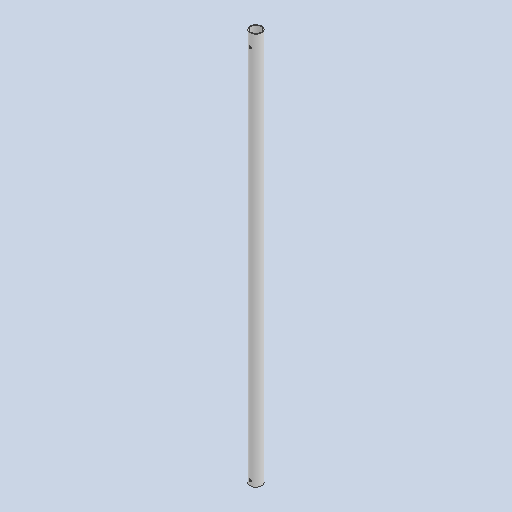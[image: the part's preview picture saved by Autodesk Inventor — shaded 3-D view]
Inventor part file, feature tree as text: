
AUTODESK INVENTOR PART (.ipt)
format: ipt  version: 2022 (Build 260153000, 153)  size: 155,648 bytes
history: native  units: mm
features: extrude x2, sketch x2
ambient origin geometry x8: Origin, YZ Plane, XZ Plane, XY Plane, X Axis, Y Axis, Z Axis, Center Point
bodies: Body1 (feature_tree)
feature tree (4):
  extrude  "Extrusion5"  Depth=15.0mm
  extrude  "Extrusion6"  Depth=10.0mm TaperAngle=0.0deg
  sketch  "Sketch2"  dims[d31=34.456mm d91=15.0mm]
  sketch  "Sketch3"  dims[d92=13.0mm d93=500.0mm d94=0.0mm d95=6.0mm d96=3.0mm d97=20.0mm d98=10.0mm d99=0.0mm d100=0.0mm d101=16.0mm d102=3.0mm]
